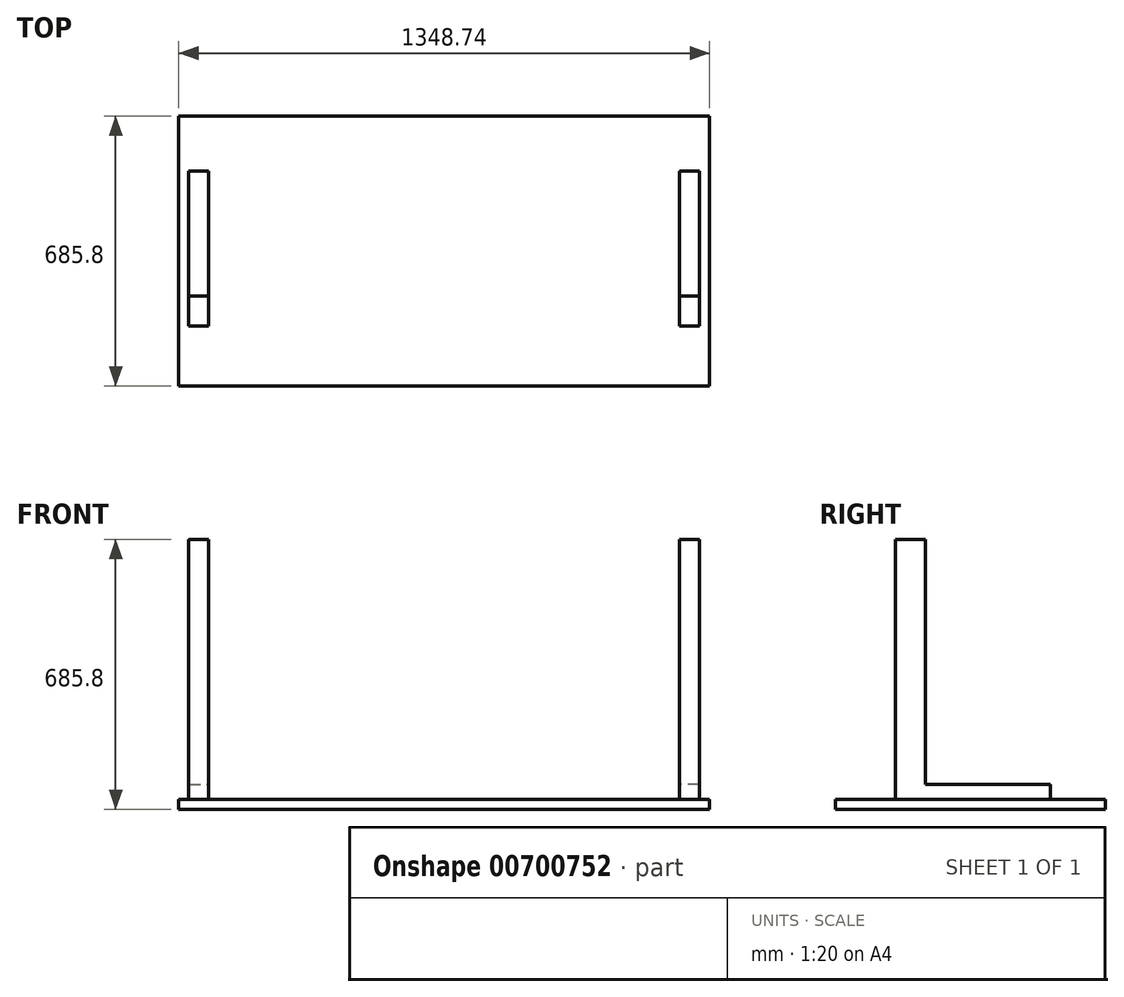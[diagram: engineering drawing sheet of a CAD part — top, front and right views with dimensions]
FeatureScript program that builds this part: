
annotation { "Feature Type Name" : "Feature", "Feature Type Description" : "" }
export const myFeature = defineFeature(function(context is Context, id is Id, definition is map)
    precondition{}
    {
        {
            var Q0;
            Q0=qCreatedBy(makeId("Top.planeOp"),FACE);
            var sketch = newSketch(context, id + "F0", { "sketchPlane" : qUnion([Q0])});
            skLineSegment(sketch, "E0.bottom", {"start": v(674.37, 342.9) * mm, "end": v(-674.37, 342.9) * mm});
            skLineSegment(sketch, "E0.top", {"start": v(674.37, -342.9) * mm, "end": v(-674.37, -342.9) * mm});
            skLineSegment(sketch, "E0.left", {"start": v(674.37, 342.9) * mm, "end": v(674.37, -342.9) * mm});
            skLineSegment(sketch, "E0.right", {"start": v(-674.37, 342.9) * mm, "end": v(-674.37, -342.9) * mm});
            skPoint(sketch, "E0.middle", {"position": v(0, 0) * mm});
            skSolve(sketch);
        }
        {
            var Q0;
            Q0=makeQuery(id+"F0.imprint","IMPRINT",FACE,{"disambiguationData":[TD([[makeQuery(id+"F0.imprint","IMPRINT",EDGE,{"derivedFrom":sQuery(id+"F0.wireOp",EDGE,"E0.bottom")}),1.0]])]});
            extrude(context, id + "F1", {"entities" : qUnion([Q0]), "depth" : 25.4 * mm, "offsetDistance" : 25.4 * mm});
        }
        {
            var Q0;
            Q0=makeQuery(id+"F1.opExtrude","CAP_FACE",FACE,{"disambiguationData":[OSD([sQuery(id+"F0.wireOp",EDGE,"E0.bottom"),sQuery(id+"F0.wireOp",EDGE,"E0.top"),sQuery(id+"F0.wireOp",EDGE,"E0.left"),sQuery(id+"F0.wireOp",EDGE,"E0.right")])],"isStart":false});
            var sketch = newSketch(context, id + "F2", { "sketchPlane" : qUnion([Q0])});
            skLineSegment(sketch, "E1", {"start": v(0, 0) * mm, "end": v(0, 342.9) * mm});
            skLineSegment(sketch, "E2", {"start": v(0, 342.9) * mm, "end": v(0, -342.9) * mm});
            skSolve(sketch);
        }
        {
            var Q0;
            {var subQ0=makeQuery(id+"F1.opExtrude","CAP_EDGE",EDGE,{"disambiguationData":[OSD([sQuery(id+"F0.wireOp",EDGE,"E0.right")])],"isStart":false});Q0=makeQuery(id+"F2.imprint","IMPRINT",FACE,{"disambiguationData":[TD([[makeQuery(id+"F2.imprint","IMPRINT",EDGE,{"derivedFrom":subQ0}),1.0]])]});}
            var sketch = newSketch(context, id + "F3", { "sketchPlane" : qUnion([Q0])});
            skLineSegment(sketch, "E3.bottom", {"start": v(-648.97, 203.2) * mm, "end": v(-598.17, 203.2) * mm});
            skLineSegment(sketch, "E3.top", {"start": v(-648.97, -114.3) * mm, "end": v(-598.17, -114.3) * mm});
            skLineSegment(sketch, "E3.left", {"start": v(-648.97, 203.2) * mm, "end": v(-648.97, -114.3) * mm});
            skLineSegment(sketch, "E3.right", {"start": v(-598.17, 203.2) * mm, "end": v(-598.17, -114.3) * mm});
            skLineSegment(sketch, "E4.MirrorCS", {"start": v(598.17, 203.2) * mm, "end": v(598.17, -114.3) * mm});
            skLineSegment(sketch, "E5.MirrorCS", {"start": v(648.97, -114.3) * mm, "end": v(598.17, -114.3) * mm});
            skLineSegment(sketch, "E6.MirrorCS", {"start": v(648.97, 203.2) * mm, "end": v(648.97, -114.3) * mm});
            skLineSegment(sketch, "E7.MirrorCS", {"start": v(648.97, 203.2) * mm, "end": v(598.17, 203.2) * mm});
            skSolve(sketch);
        }
        {
            var Q0;
            Q0 = qSketchRegion(id + "F3", true);
            extrude(context, id + "F4", {"entities" : qUnion([Q0]), "operationType" : NewBodyOperationType.ADD, "depth" : 38.1 * mm, "offsetDistance" : 25.4 * mm});
        }
        {
            var Q0;
            {var subQ0=makeQuery(id+"F1.opExtrude","CAP_EDGE",EDGE,{"disambiguationData":[OSD([sQuery(id+"F0.wireOp",EDGE,"E0.right")])],"isStart":false});Q0=makeQuery(id+"F2.imprint","IMPRINT",FACE,{"disambiguationData":[TD([[makeQuery(id+"F2.imprint","IMPRINT",EDGE,{"derivedFrom":subQ0}),1.0]])]});}
            var sketch = newSketch(context, id + "F5", { "sketchPlane" : qUnion([Q0])});
            skLineSegment(sketch, "E8.bottom", {"start": v(-648.97, -114.3) * mm, "end": v(-598.17, -114.3) * mm});
            skLineSegment(sketch, "E8.top", {"start": v(-648.97, -190.5) * mm, "end": v(-598.17, -190.5) * mm});
            skLineSegment(sketch, "E8.left", {"start": v(-648.97, -114.3) * mm, "end": v(-648.97, -190.5) * mm});
            skLineSegment(sketch, "E8.right", {"start": v(-598.17, -114.3) * mm, "end": v(-598.17, -190.5) * mm});
            skLineSegment(sketch, "E9.MirrorCS", {"start": v(598.17, -114.3) * mm, "end": v(598.17, -190.5) * mm});
            skLineSegment(sketch, "E10.MirrorCS", {"start": v(648.97, -190.5) * mm, "end": v(598.17, -190.5) * mm});
            skLineSegment(sketch, "E11.MirrorCS", {"start": v(648.97, -114.3) * mm, "end": v(648.97, -190.5) * mm});
            skLineSegment(sketch, "E12.MirrorCS", {"start": v(648.97, -114.3) * mm, "end": v(598.17, -114.3) * mm});
            skSolve(sketch);
        }
        {
            var Q0;
            Q0 = qSketchRegion(id + "F5", true);
            extrude(context, id + "F6", {"entities" : qUnion([Q0]), "operationType" : NewBodyOperationType.ADD, "depth" : 660.4 * mm, "offsetDistance" : 25.4 * mm});
        }
    });
